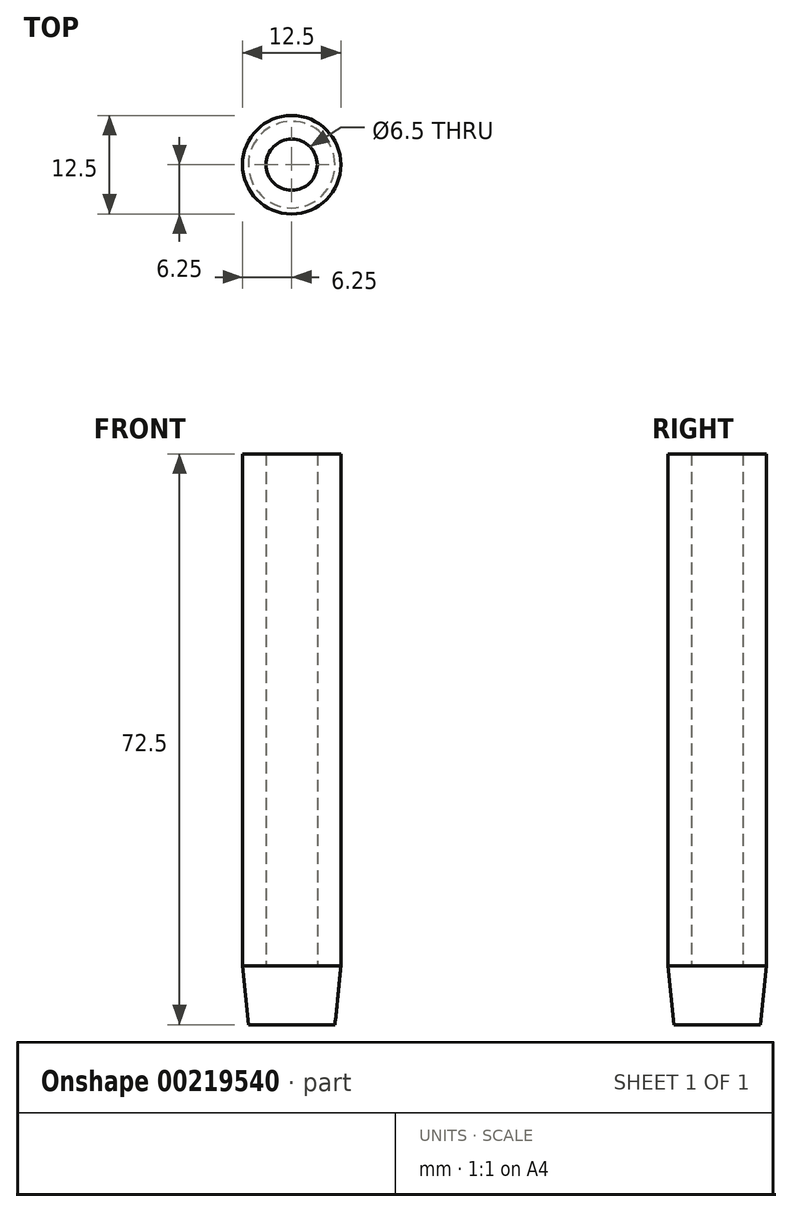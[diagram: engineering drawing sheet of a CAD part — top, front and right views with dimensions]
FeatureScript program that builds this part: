
annotation { "Feature Type Name" : "Feature", "Feature Type Description" : "" }
export const myFeature = defineFeature(function(context is Context, id is Id, definition is map)
    precondition{}
    {
        {
            var Q0;
            Q0=qCreatedBy(makeId("Top.planeOp"),FACE);
            var sketch = newSketch(context, id + "F0", { "sketchPlane" : qUnion([Q0])});
            skCircle(sketch, "E0", {"center": v(0, 0) * mm, "radius": 6.25 * mm});
            skSolve(sketch);
        }
        {
            var Q0;
            Q0=qCreatedBy(makeId("Top.planeOp"),FACE);
            var sketch = newSketch(context, id + "F1", { "sketchPlane" : qUnion([Q0])});
            skCircle(sketch, "E1", {"center": v(0, 0) * mm, "radius": 3.25 * mm});
            skSolve(sketch);
        }
        {
            var Q0;
            Q0=qCreatedBy(makeId("Top.planeOp"),FACE);
            cPlane(context, id + "F2", {"entities" : qUnion([Q0]), "cplaneType" : CPlaneType.OFFSET, "offset" : 7.5 * mm, "oppositeDirection" : true, "width" : 150 * mm, "height" : 150 * mm});
        }
        {
            var Q0;
            Q0=qCreatedBy(id+"F2.planeOp",FACE);
            var sketch = newSketch(context, id + "F3", { "sketchPlane" : qUnion([Q0])});
            skCircle(sketch, "E2", {"center": v(0, 0) * mm, "radius": 5.5 * mm});
            skSolve(sketch);
        }
        {
            var Q0;
            Q0 = qSketchRegion(id + "F0", true);
            var Q1;
            Q1 = qSketchRegion(id + "F3", true);
            loft(context, id + "F4", {"sheetProfilesArray" : [{ "sheetProfileEntities" : qUnion([Q0]) }, { "sheetProfileEntities" : qUnion([Q1]) }]});
        }
        {
            var Q0;
            Q0=makeQuery(id+"F0.imprint","IMPRINT",FACE,{"disambiguationData":[TD([[makeQuery(id+"F0.imprint","IMPRINT",EDGE,{"derivedFrom":sQuery(id+"F0.wireOp",EDGE,"E0")}),1.0]])]});
            extrude(context, id + "F5", {"entities" : qUnion([Q0]), "depth" : 65 * mm});
        }
        {
            var Q0;
            Q0 = qSketchRegion(id + "F1", true);
            extrude(context, id + "F6", {"entities" : qUnion([Q0]), "operationType" : NewBodyOperationType.REMOVE, "depth" : 65 * mm});
        }
    });
